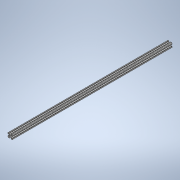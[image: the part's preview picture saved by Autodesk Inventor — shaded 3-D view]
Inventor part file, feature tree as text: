
AUTODESK INVENTOR PART (.ipt)
format: ipt  version: 2020 (Build 240168000, 168)  size: 245,248 bytes
history: native  units: in
note: dims shown in document units (in); Inventor stores cm internally (conversion verified against a paired STEP export)
features: extrude x1, sketch x1
ambient origin geometry x8: Origin, YZ Plane, XZ Plane, XY Plane, X Axis, Y Axis, Z Axis, Center Point
bodies: Solid1 (feature_tree)
feature tree (2):
  extrude  "Extrusion1"  Depth=35.0in
  sketch  "Sketch1"  dims[d0=35.0in d1=0.0in d2=0.5in d3=0.0344in d4=0.5in d5=0.0344in]
